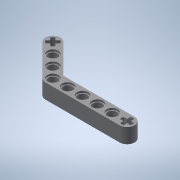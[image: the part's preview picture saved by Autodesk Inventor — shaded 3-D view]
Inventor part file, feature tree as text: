
AUTODESK INVENTOR PART (.ipt)
format: ipt  version: 2021 (Build 250183000, 183)  size: 265,728 bytes
history: native  units: mm
features: extrude x8, sketch x8
ambient origin geometry x8: Origin, YZ Plane, XZ Plane, XY Plane, X Axis, Y Axis, Z Axis, Center Point
bodies: Solid1 (feature_tree)
feature tree (16):
  extrude  "Extrusion1"  TaperAngle=0.0deg  [1 undecoded]
  extrude  "Extrusion2"  Depth=4.0mm
  extrude  "Extrusion3"  Depth=40.0mm
  extrude  "Extrusion10"  Depth=4.0mm
  extrude  "Extrusion11"  Depth=8.0mm TaperAngle=0.0deg
  extrude  "Extrusion12"  Depth=3.0mm
  extrude  "Extrusion13"  Depth=3.0mm
  extrude  "Extrusion14"  Depth=2.0mm
  sketch  "Sketch1"  dims[d13=4.0mm d15=0.0mm]
  sketch  "Sketch2"  dims[d16=0.0mm d25=4.0mm]
  sketch  "Sketch3"  dims[d27=135.0deg d29=40.0mm]
  sketch  "Sketch10"  dims[d35=135.0deg d36=4.0mm]
  sketch  "Sketch11"  dims[d37=24.0mm d39=8.0mm d40=0.0mm]
  sketch  "Sketch12"  dims[d46=3.0mm d47=3.0mm]
  sketch  "Sketch13"  dims[d48=3.0mm d49=3.0mm]
  sketch  "Sketch14"  dims[d50=2.0mm d51=2.0mm d52=2.0mm d53=2.0mm d54=1.0mm d55=1.0mm d56=1.0mm d57=1.0mm d58=90.0deg d59=90.0deg d60=90.0deg d61=90.0deg d62=8.0mm d63=0.0mm d64=6.0mm d65=3.0mm d66=3.0mm d67=3.0mm d68=3.0mm d69=2.0mm d70=2.0mm d71=2.0mm d72=2.0mm d73=90.0deg d74=90.0deg d75=90.0deg d76=1.0mm d77=1.0mm d78=1.0mm d79=1.0mm d80=2.828427mm d81=8.0mm d82=0.0mm d142=24.0mm d143=5.0mm d144=8.0mm d145=0.0mm d146=0.0mm d147=0.0mm d148=50.0mm d150=8.0mm d151=10.0mm d153=10.0mm d155=5.0mm d157=4.0mm d158=8.0mm d159=20.0mm d161=8.0mm d162=10.0mm d164=10.0mm d166=0.0mm d167=0.0mm d168=6.0mm d169=50.0mm d171=8.0mm d172=10.0mm d174=10.0mm d176=1.0mm d177=0.0mm d178=6.0mm d179=6.0mm d180=1.0mm d181=0.0mm d182=6.0mm d183=6.0mm d184=6.0mm d185=50.0mm d187=8.0mm d188=10.0mm d190=10.0mm d192=1.0mm d193=0.0mm]
note: 1 required parameter value undecoded (feature->parameter linkage not recoverable at this tier; creation-order binding heuristic only, values carry confidence <= 0.55)
